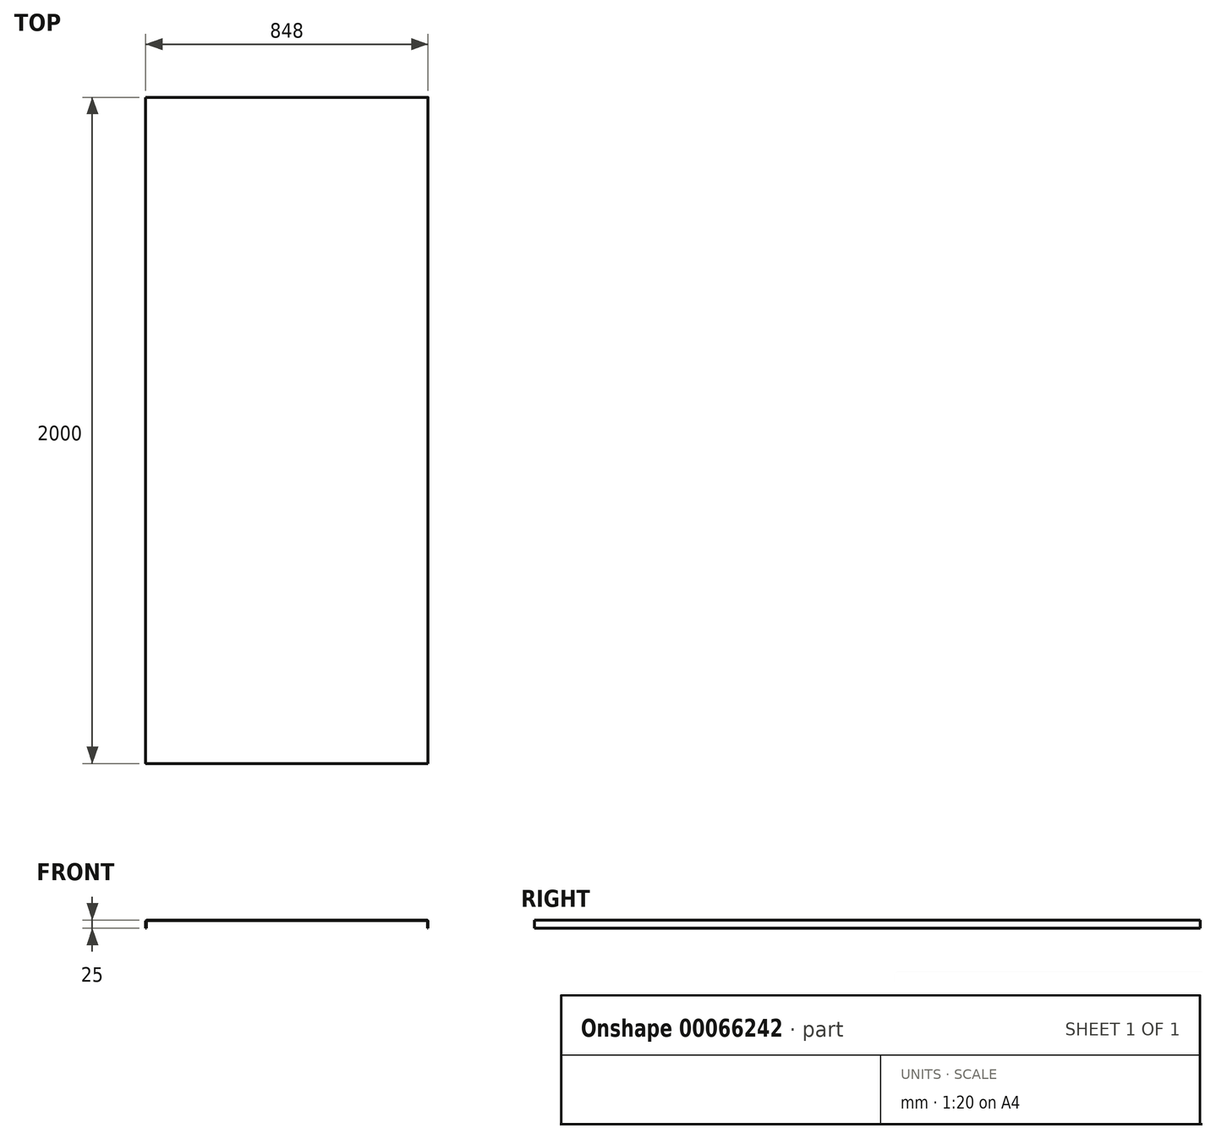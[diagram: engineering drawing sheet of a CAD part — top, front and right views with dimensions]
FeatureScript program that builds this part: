
annotation { "Feature Type Name" : "Feature", "Feature Type Description" : "" }
export const myFeature = defineFeature(function(context is Context, id is Id, definition is map)
    precondition{}
    {
        {
            var Q0;
            Q0=qCreatedBy(makeId("Front.planeOp"),FACE);
            var sketch = newSketch(context, id + "F0", { "sketchPlane" : qUnion([Q0])});
            skLineSegment(sketch, "E0", {"start": v(-52.93, 4.7) * mm, "end": v(-52.93, 25.7) * mm});
            skLineSegment(sketch, "E1", {"start": v(-50.43, 28.2) * mm, "end": v(789.57, 28.2) * mm});
            skLineSegment(sketch, "E2", {"start": v(792.07, 25.7) * mm, "end": v(792.07, 4.7) * mm});
            skLineSegment(sketch, "E3.0", {"start": v(-54.43, 4.7) * mm, "end": v(-54.43, 25.7) * mm});
            skLineSegment(sketch, "E4.0", {"start": v(-50.43, 29.7) * mm, "end": v(789.57, 29.7) * mm});
            skLineSegment(sketch, "E5.0", {"start": v(793.57, 25.7) * mm, "end": v(793.57, 4.7) * mm});
            skPoint(sketch, "E6.visualSharp", {"position": v(-52.93, 28.2) * mm});
            skArc(sketch, "E6.filletArc", {"start": v(-50.43, 28.2) * mm, "mid": v(-52.2, 27.47) * mm, "end": v(-52.93, 25.7) * mm});
            skPoint(sketch, "E7.visualSharp", {"position": v(792.07, 28.2) * mm});
            skArc(sketch, "E7.filletArc", {"start": v(792.07, 25.7) * mm, "mid": v(791.34, 27.47) * mm, "end": v(789.57, 28.2) * mm});
            skArc(sketch, "E8.filletArc", {"start": v(-50.43, 29.7) * mm, "mid": v(-53.26, 28.53) * mm, "end": v(-54.43, 25.7) * mm});
            skArc(sketch, "E9.filletArc", {"start": v(793.57, 25.7) * mm, "mid": v(792.4, 28.53) * mm, "end": v(789.57, 29.7) * mm});
            skLineSegment(sketch, "E10", {"start": v(792.07, 4.7) * mm, "end": v(793.57, 4.7) * mm});
            skLineSegment(sketch, "E11", {"start": v(-54.43, 4.7) * mm, "end": v(-52.93, 4.7) * mm});
            skSolve(sketch);
        }
        {
            var Q0;
            Q0=makeQuery(id+"F0.imprint","IMPRINT",FACE,{"disambiguationData":[TD([[makeQuery(id+"F0.imprint","IMPRINT",EDGE,{"derivedFrom":sQuery(id+"F0.wireOp",EDGE,"E0")}),1.0]])]});
            extrude(context, id + "F1", {"entities" : qUnion([Q0]), "depth" : 2000 * mm});
        }
    });
